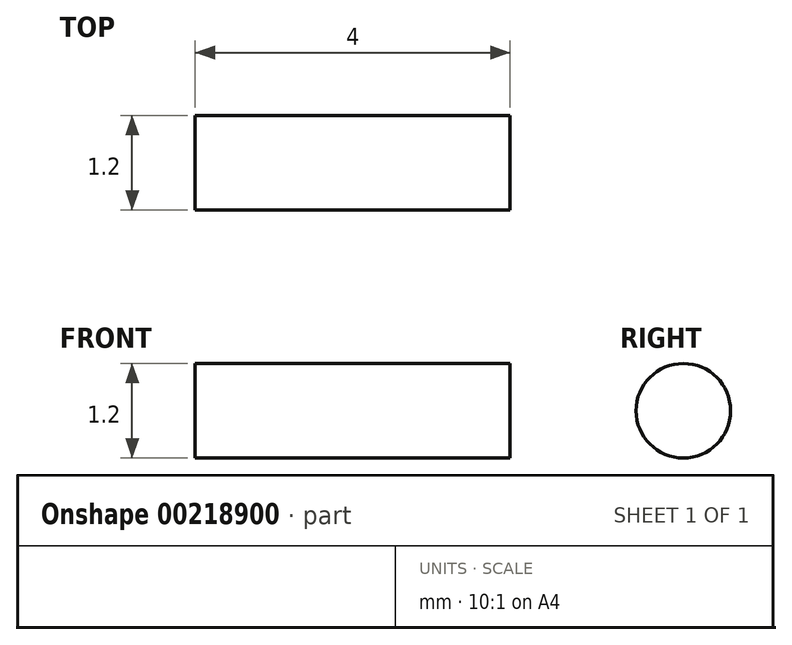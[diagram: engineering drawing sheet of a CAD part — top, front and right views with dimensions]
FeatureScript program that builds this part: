
annotation { "Feature Type Name" : "Feature", "Feature Type Description" : "" }
export const myFeature = defineFeature(function(context is Context, id is Id, definition is map)
    precondition{}
    {
        {
            var Q0;
            Q0=qCreatedBy(makeId("Right.planeOp"),FACE);
            var sketch = newSketch(context, id + "F0", { "sketchPlane" : qUnion([Q0])});
            skCircle(sketch, "E0", {"center": v(0, 0) * mm, "radius": 0.6 * mm});
            skSolve(sketch);
        }
        {
            var Q0;
            Q0=qSketchRegion(id+"F0",true);
            extrude(context, id + "F1", {"entities" : qUnion([Q0]), "oppositeDirection" : true, "depth" : 4 * mm});
        }
    });
